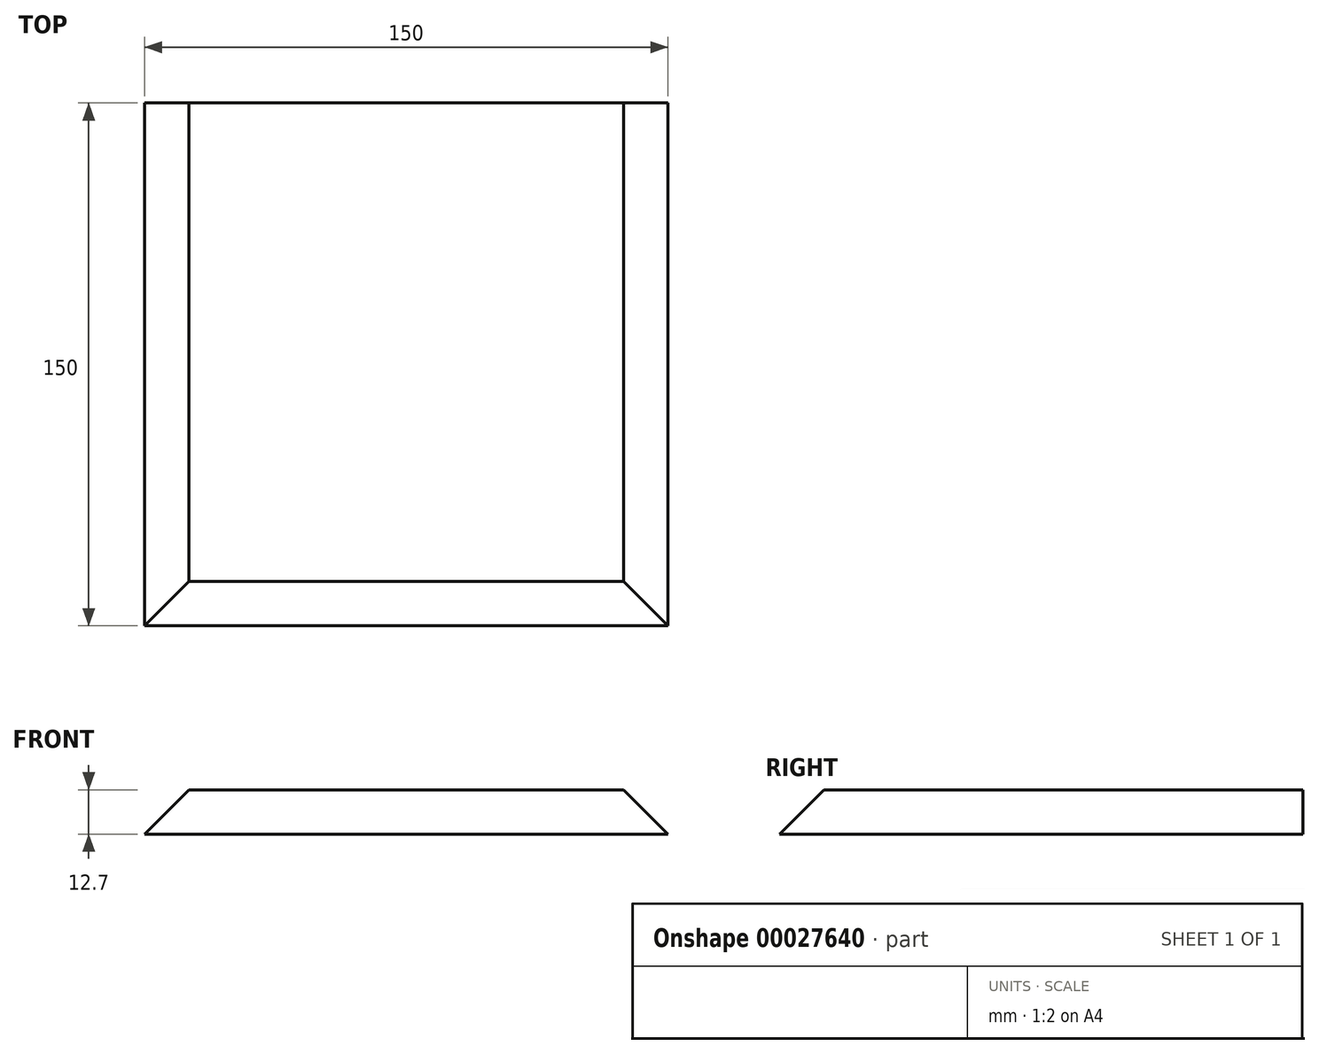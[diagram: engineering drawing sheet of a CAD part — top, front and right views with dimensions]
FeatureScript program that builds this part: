
annotation { "Feature Type Name" : "Feature", "Feature Type Description" : "" }
export const myFeature = defineFeature(function(context is Context, id is Id, definition is map)
    precondition{}
    {
        {
            var Q0;
            Q0=qCreatedBy(makeId("Top.planeOp"),FACE);
            var sketch = newSketch(context, id + "F0", { "sketchPlane" : qUnion([Q0])});
            skLineSegment(sketch, "E0.rect.bottom", {"start": v(-75, -75) * mm, "end": v(75, -75) * mm});
            skLineSegment(sketch, "E0.rect.top", {"start": v(-75, 75) * mm, "end": v(75, 75) * mm});
            skLineSegment(sketch, "E0.rect.left", {"start": v(-75, -75) * mm, "end": v(-75, 75) * mm});
            skLineSegment(sketch, "E0.rect.right", {"start": v(75, -75) * mm, "end": v(75, 75) * mm});
            skPoint(sketch, "E0.rect.middle", {"position": v(0, 0) * mm});
            skSolve(sketch);
        }
        {
            var Q0;
            Q0=makeQuery(id+"F0.imprint","IMPRINT",FACE,{"disambiguationData":[TD([[makeQuery(id+"F0.imprint","IMPRINT",EDGE,{"derivedFrom":sQuery(id+"F0.wireOp",EDGE,"E0.rect.bottom")}),1.0]])]});
            extrude(context, id + "F1", {"entities" : qUnion([Q0]), "depth" : 12.7 * mm});
        }
        {
            var Q0;
            Q0=makeQuery(id+"F1.opExtrude","CAP_EDGE",EDGE,{"disambiguationData":[OSD([sQuery(id+"F0.wireOp",EDGE,"E0.rect.right")])],"isStart":false});
            var Q1;
            Q1=makeQuery(id+"F1.opExtrude","CAP_EDGE",EDGE,{"disambiguationData":[OSD([sQuery(id+"F0.wireOp",EDGE,"E0.rect.bottom")])],"isStart":false});
            var Q2;
            Q2=makeQuery(id+"F1.opExtrude","CAP_EDGE",EDGE,{"disambiguationData":[OSD([sQuery(id+"F0.wireOp",EDGE,"E0.rect.left")])],"isStart":false});
            chamfer(context, id + "F2", {"entities" : qUnion([Q0, Q1, Q2]), "width" : 12.7 * mm, "tangentPropagation" : true});
        }
    });
